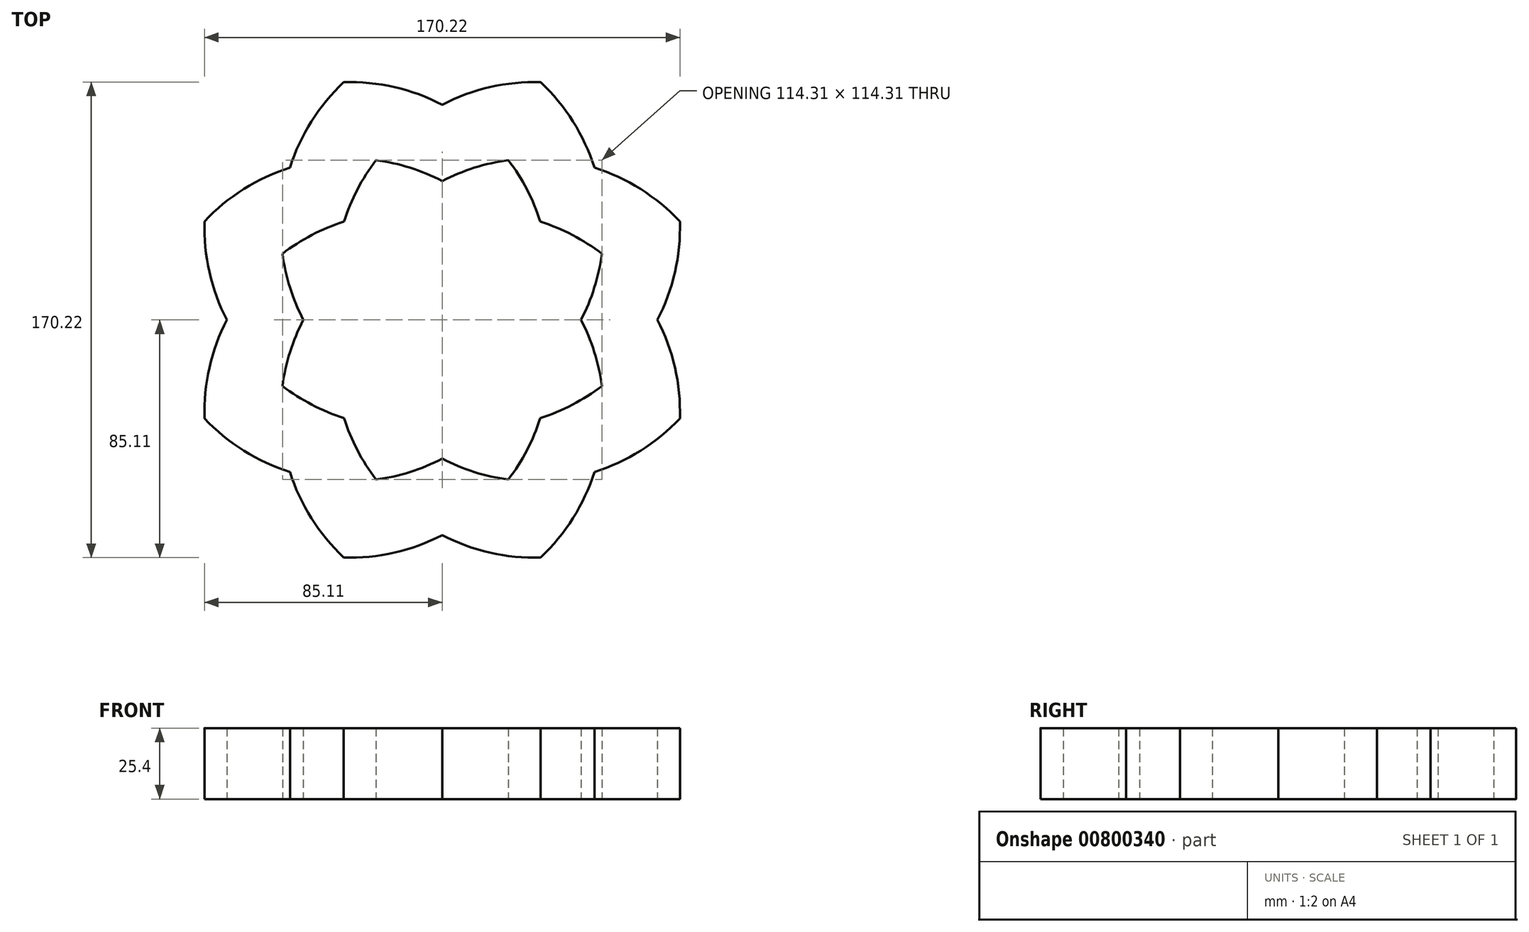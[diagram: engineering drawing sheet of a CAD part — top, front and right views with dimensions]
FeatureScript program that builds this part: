
annotation { "Feature Type Name" : "Feature", "Feature Type Description" : "" }
export const myFeature = defineFeature(function(context is Context, id is Id, definition is map)
    precondition{}
    {
        {
            var Q0;
            Q0=qCreatedBy(makeId("Top.planeOp"),FACE);
            var sketch = newSketch(context, id + "F0", { "sketchPlane" : qUnion([Q0])});
            skCircle(sketch, "E0.cCircle", {"center": v(0, 0) * mm, "radius": 38.66 * mm, "construction": true});
            skLineSegment(sketch, "E0.0", {"start": v(38.66, 0) * mm, "end": v(27.34, -27.34) * mm});
            skLineSegment(sketch, "E0.1", {"start": v(27.34, -27.34) * mm, "end": v(0, -38.66) * mm});
            skLineSegment(sketch, "E0.2", {"start": v(0, -38.66) * mm, "end": v(-27.34, -27.34) * mm});
            skLineSegment(sketch, "E0.3", {"start": v(-27.34, -27.34) * mm, "end": v(-38.66, 0) * mm});
            skLineSegment(sketch, "E0.4", {"start": v(-38.66, 0) * mm, "end": v(-27.34, 27.34) * mm});
            skLineSegment(sketch, "E0.5", {"start": v(-27.34, 27.34) * mm, "end": v(0, 38.66) * mm});
            skLineSegment(sketch, "E0.6", {"start": v(0, 38.66) * mm, "end": v(27.34, 27.34) * mm});
            skLineSegment(sketch, "E0.7", {"start": v(27.34, 27.34) * mm, "end": v(38.66, 0) * mm});
            skCircle(sketch, "E1", {"center": v(13.67, 33) * mm, "radius": 71.44 * mm});
            skCircle(sketch, "E2", {"center": v(-13.67, -33) * mm, "radius": 71.44 * mm});
            skCircle(sketch, "E3", {"center": v(13.67, -33) * mm, "radius": 71.44 * mm});
            skCircle(sketch, "E4", {"center": v(-13.67, 33) * mm, "radius": 71.44 * mm});
            skCircle(sketch, "E5", {"center": v(33, -13.67) * mm, "radius": 71.44 * mm});
            skCircle(sketch, "E6", {"center": v(-33, 13.67) * mm, "radius": 71.44 * mm});
            skCircle(sketch, "E7", {"center": v(33, 13.67) * mm, "radius": 71.44 * mm});
            skCircle(sketch, "E8", {"center": v(-33, -13.67) * mm, "radius": 71.44 * mm});
            skSolve(sketch);
        }
        {
            var Q0;
            {var subQ0=sQuery(id+"F0.wireOp",EDGE,"E2");var subQ1=sQuery(id+"F0.wireOp",EDGE,"E1");var subQ2=makeQuery(id+"F0.imprint","INTERSECT",VERTEX,{"disambiguationData":[OD(1.0)],"derivedFrom":[subQ1,subQ0]});Q0=makeQuery(id+"F0.imprint","IMPRINT",FACE,{"disambiguationData":[TD([[makeQuery(id+"F0.imprint","IMPRINT",EDGE,{"disambiguationData":[TD([[subQ2,-1.0]])],"derivedFrom":subQ1}),-1.0]])]});}
            var Q1;
            {var subQ0=sQuery(id+"F0.wireOp",EDGE,"E8");var subQ1=sQuery(id+"F0.wireOp",EDGE,"E1");var subQ2=makeQuery(id+"F0.imprint","INTERSECT",VERTEX,{"disambiguationData":[OD(1.0)],"derivedFrom":[subQ1,subQ0]});Q1=makeQuery(id+"F0.imprint","IMPRINT",FACE,{"disambiguationData":[TD([[makeQuery(id+"F0.imprint","IMPRINT",EDGE,{"disambiguationData":[TD([[subQ2,-1.0]])],"derivedFrom":subQ1}),-1.0]])]});}
            var Q2;
            {var subQ0=sQuery(id+"F0.wireOp",EDGE,"E2");var subQ1=sQuery(id+"F0.wireOp",EDGE,"E1");var subQ2=makeQuery(id+"F0.imprint","INTERSECT",VERTEX,{"disambiguationData":[OD(1.0)],"derivedFrom":[subQ1,subQ0]});Q2=makeQuery(id+"F0.imprint","IMPRINT",FACE,{"disambiguationData":[TD([[makeQuery(id+"F0.imprint","IMPRINT",EDGE,{"disambiguationData":[TD([[subQ2,-1.0]])],"derivedFrom":subQ1}),1.0]])]});}
            var Q3;
            {var subQ0=sQuery(id+"F0.wireOp",EDGE,"E6");var subQ1=sQuery(id+"F0.wireOp",EDGE,"E5");var subQ2=makeQuery(id+"F0.imprint","INTERSECT",VERTEX,{"disambiguationData":[OD(0.0)],"derivedFrom":[subQ1,subQ0]});Q3=makeQuery(id+"F0.imprint","IMPRINT",FACE,{"disambiguationData":[TD([[makeQuery(id+"F0.imprint","IMPRINT",EDGE,{"disambiguationData":[TD([[subQ2,-1.0]])],"derivedFrom":subQ1}),-1.0]])]});}
            var Q4;
            {var subQ0=sQuery(id+"F0.wireOp",EDGE,"E5");var subQ1=sQuery(id+"F0.wireOp",EDGE,"E1");var subQ2=makeQuery(id+"F0.imprint","INTERSECT",VERTEX,{"disambiguationData":[OD(0.0)],"derivedFrom":[subQ1,subQ0]});Q4=makeQuery(id+"F0.imprint","IMPRINT",FACE,{"disambiguationData":[TD([[makeQuery(id+"F0.imprint","IMPRINT",EDGE,{"disambiguationData":[TD([[subQ2,1.0]])],"derivedFrom":subQ1}),1.0]])]});}
            var Q5;
            {var subQ0=sQuery(id+"F0.wireOp",EDGE,"E4");var subQ1=sQuery(id+"F0.wireOp",EDGE,"E3");var subQ2=makeQuery(id+"F0.imprint","INTERSECT",VERTEX,{"disambiguationData":[OD(0.0)],"derivedFrom":[subQ1,subQ0]});Q5=makeQuery(id+"F0.imprint","IMPRINT",FACE,{"disambiguationData":[TD([[makeQuery(id+"F0.imprint","IMPRINT",EDGE,{"disambiguationData":[TD([[subQ2,-1.0]])],"derivedFrom":subQ1}),-1.0]])]});}
            var Q6;
            {var subQ0=sQuery(id+"F0.wireOp",EDGE,"E6");var subQ1=sQuery(id+"F0.wireOp",EDGE,"E1");var subQ2=makeQuery(id+"F0.imprint","INTERSECT",VERTEX,{"disambiguationData":[OD(0.0)],"derivedFrom":[subQ1,subQ0]});Q6=makeQuery(id+"F0.imprint","IMPRINT",FACE,{"disambiguationData":[TD([[makeQuery(id+"F0.imprint","IMPRINT",EDGE,{"disambiguationData":[TD([[subQ2,-1.0]])],"derivedFrom":subQ1}),1.0]])]});}
            var Q7;
            {var subQ0=sQuery(id+"F0.wireOp",EDGE,"E7");var subQ1=sQuery(id+"F0.wireOp",EDGE,"E4");var subQ2=makeQuery(id+"F0.imprint","INTERSECT",VERTEX,{"disambiguationData":[OD(0.0)],"derivedFrom":[subQ1,subQ0]});Q7=makeQuery(id+"F0.imprint","IMPRINT",FACE,{"disambiguationData":[TD([[makeQuery(id+"F0.imprint","IMPRINT",EDGE,{"disambiguationData":[TD([[subQ2,1.0]])],"derivedFrom":subQ1}),1.0]])]});}
            var Q8;
            {var subQ0=sQuery(id+"F0.wireOp",EDGE,"E8");var subQ1=sQuery(id+"F0.wireOp",EDGE,"E1");var subQ2=makeQuery(id+"F0.imprint","INTERSECT",VERTEX,{"disambiguationData":[OD(0.0)],"derivedFrom":[subQ1,subQ0]});Q8=makeQuery(id+"F0.imprint","IMPRINT",FACE,{"disambiguationData":[TD([[makeQuery(id+"F0.imprint","IMPRINT",EDGE,{"disambiguationData":[TD([[subQ2,-1.0]])],"derivedFrom":subQ1}),1.0]])]});}
            var Q9;
            {var subQ0=sQuery(id+"F0.wireOp",EDGE,"E4");var subQ1=sQuery(id+"F0.wireOp",EDGE,"E2");var subQ2=makeQuery(id+"F0.imprint","INTERSECT",VERTEX,{"disambiguationData":[OD(1.0)],"derivedFrom":[subQ1,subQ0]});Q9=makeQuery(id+"F0.imprint","IMPRINT",FACE,{"disambiguationData":[TD([[makeQuery(id+"F0.imprint","IMPRINT",EDGE,{"disambiguationData":[TD([[subQ2,-1.0]])],"derivedFrom":subQ1}),1.0]])]});}
            var Q10;
            {var subQ0=sQuery(id+"F0.wireOp",EDGE,"E8");var subQ1=sQuery(id+"F0.wireOp",EDGE,"E1");var subQ2=makeQuery(id+"F0.imprint","INTERSECT",VERTEX,{"disambiguationData":[OD(0.0)],"derivedFrom":[subQ1,subQ0]});Q10=makeQuery(id+"F0.imprint","IMPRINT",FACE,{"disambiguationData":[TD([[makeQuery(id+"F0.imprint","IMPRINT",EDGE,{"disambiguationData":[TD([[subQ2,-1.0]])],"derivedFrom":subQ1}),-1.0]])]});}
            var Q11;
            {var subQ0=sQuery(id+"F0.wireOp",EDGE,"E2");var subQ1=sQuery(id+"F0.wireOp",EDGE,"E1");var subQ2=makeQuery(id+"F0.imprint","INTERSECT",VERTEX,{"disambiguationData":[OD(0.0)],"derivedFrom":[subQ1,subQ0]});Q11=makeQuery(id+"F0.imprint","IMPRINT",FACE,{"disambiguationData":[TD([[makeQuery(id+"F0.imprint","IMPRINT",EDGE,{"disambiguationData":[TD([[subQ2,-1.0]])],"derivedFrom":subQ1}),-1.0]])]});}
            var Q12;
            {var subQ0=sQuery(id+"F0.wireOp",EDGE,"E6");var subQ1=sQuery(id+"F0.wireOp",EDGE,"E3");var subQ2=makeQuery(id+"F0.imprint","INTERSECT",VERTEX,{"disambiguationData":[OD(1.0)],"derivedFrom":[subQ1,subQ0]});Q12=makeQuery(id+"F0.imprint","IMPRINT",FACE,{"disambiguationData":[TD([[makeQuery(id+"F0.imprint","IMPRINT",EDGE,{"disambiguationData":[TD([[subQ2,-1.0]])],"derivedFrom":subQ1}),1.0]])]});}
            var Q13;
            {var subQ0=sQuery(id+"F0.wireOp",EDGE,"E6");var subQ1=sQuery(id+"F0.wireOp",EDGE,"E5");var subQ2=makeQuery(id+"F0.imprint","INTERSECT",VERTEX,{"disambiguationData":[OD(1.0)],"derivedFrom":[subQ1,subQ0]});Q13=makeQuery(id+"F0.imprint","IMPRINT",FACE,{"disambiguationData":[TD([[makeQuery(id+"F0.imprint","IMPRINT",EDGE,{"disambiguationData":[TD([[subQ2,-1.0]])],"derivedFrom":subQ1}),1.0]])]});}
            var Q14;
            {var subQ0=sQuery(id+"F0.wireOp",EDGE,"E4");var subQ1=sQuery(id+"F0.wireOp",EDGE,"E3");var subQ2=makeQuery(id+"F0.imprint","INTERSECT",VERTEX,{"disambiguationData":[OD(1.0)],"derivedFrom":[subQ1,subQ0]});Q14=makeQuery(id+"F0.imprint","IMPRINT",FACE,{"disambiguationData":[TD([[makeQuery(id+"F0.imprint","IMPRINT",EDGE,{"disambiguationData":[TD([[subQ2,-1.0]])],"derivedFrom":subQ1}),1.0]])]});}
            var Q15;
            {var subQ0=sQuery(id+"F0.wireOp",EDGE,"E5");var subQ1=sQuery(id+"F0.wireOp",EDGE,"E2");var subQ2=makeQuery(id+"F0.imprint","INTERSECT",VERTEX,{"disambiguationData":[OD(1.0)],"derivedFrom":[subQ1,subQ0]});Q15=makeQuery(id+"F0.imprint","IMPRINT",FACE,{"disambiguationData":[TD([[makeQuery(id+"F0.imprint","IMPRINT",EDGE,{"disambiguationData":[TD([[subQ2,-1.0]])],"derivedFrom":subQ1}),1.0]])]});}
            extrude(context, id + "F1", {"entities" : qUnion([Q0, Q1, Q2, Q3, Q4, Q5, Q6, Q7, Q8, Q9, Q10, Q11, Q12, Q13, Q14, Q15]), "depth" : 25.4 * mm, "offsetDistance" : 25.4 * mm});
        }
    });
